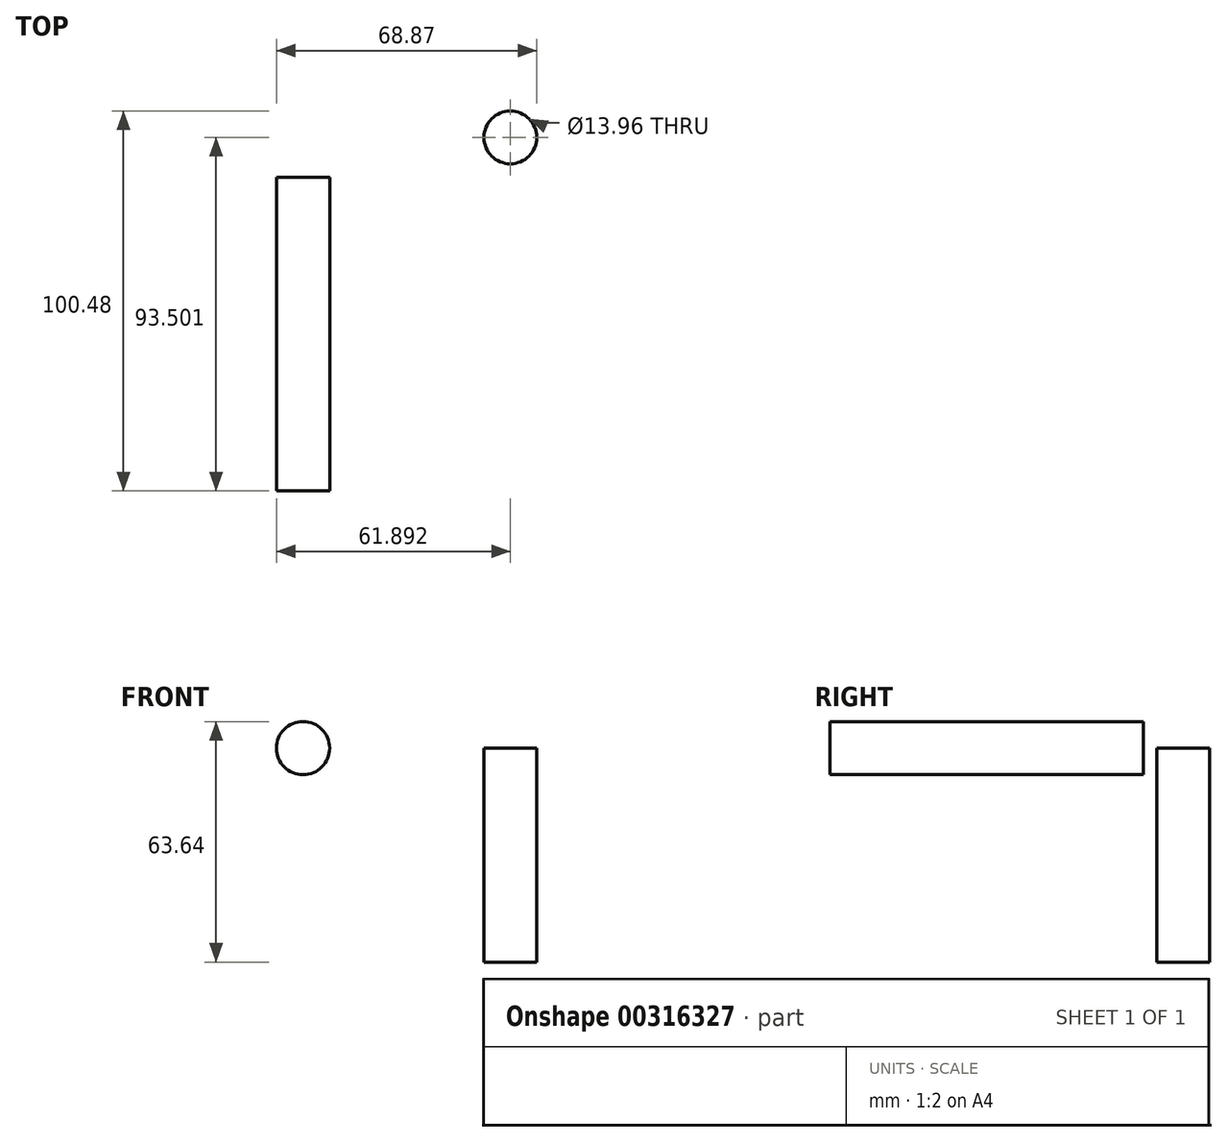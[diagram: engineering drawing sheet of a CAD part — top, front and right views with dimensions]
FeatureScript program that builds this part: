
annotation { "Feature Type Name" : "Feature", "Feature Type Description" : "" }
export const myFeature = defineFeature(function(context is Context, id is Id, definition is map)
    precondition{}
    {
        {
            var Q0;
            Q0=qCreatedBy(makeId("Front.planeOp"),FACE);
            var sketch = newSketch(context, id + "F0", { "sketchPlane" : qUnion([Q0])});
            skCircle(sketch, "E0", {"center": v(0, 0) * mm, "radius": 7.04 * mm});
            skSolve(sketch);
        }
        {
            var Q0;
            Q0=sQuery(id+"F0.wireOp",EDGE,"E0");
            extrude(context, id + "F1", {"bodyType" : ToolBodyType.SURFACE, "surfaceEntities" : qUnion([Q0]), "endBound" : BoundingType.SYMMETRIC, "depth" : 83 * mm});
        }
        {
            var Q0;
            Q0=qCreatedBy(makeId("Top.planeOp"),FACE);
            var sketch = newSketch(context, id + "F2", { "sketchPlane" : qUnion([Q0])});
            skCircle(sketch, "E1", {"center": v(54.85, 52) * mm, "radius": 6.98 * mm});
            skSolve(sketch);
        }
        {
            var Q0;
            Q0=sQuery(id+"F2.wireOp",EDGE,"E1");
            extrude(context, id + "F3", {"bodyType" : ToolBodyType.SURFACE, "surfaceEntities" : qUnion([Q0]), "oppositeDirection" : true, "depth" : 56.6 * mm});
        }
    });
